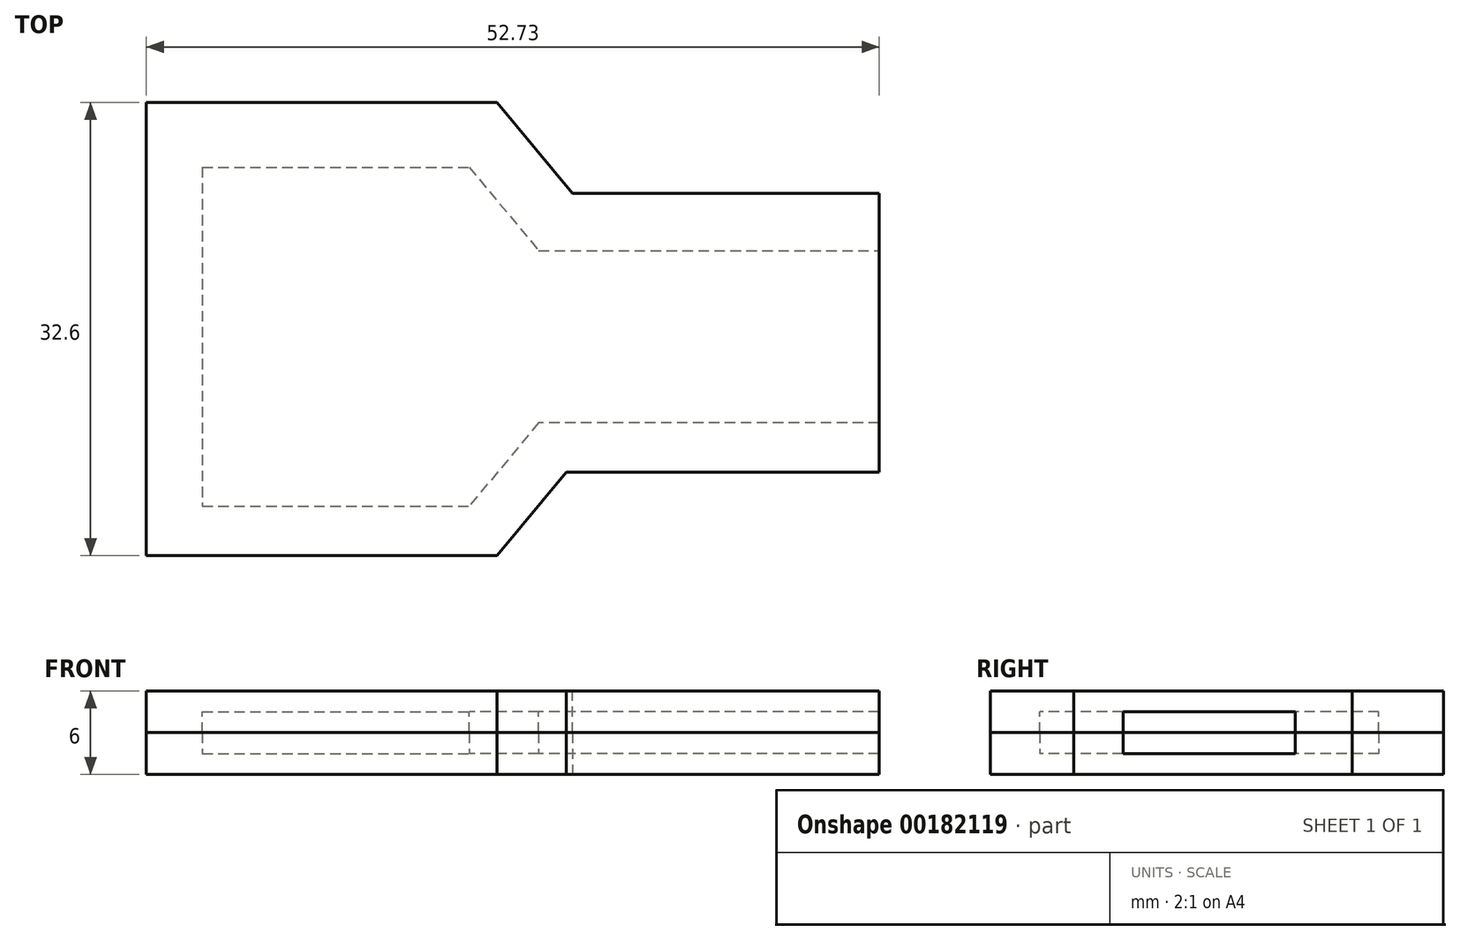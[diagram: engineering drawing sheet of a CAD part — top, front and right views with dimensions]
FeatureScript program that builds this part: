
annotation { "Feature Type Name" : "Feature", "Feature Type Description" : "" }
export const myFeature = defineFeature(function(context is Context, id is Id, definition is map)
    precondition{}
    {
        {
            var Q0;
            Q0=qCreatedBy(makeId("Top.planeOp"),FACE);
            var sketch = newSketch(context, id + "F0", { "sketchPlane" : qUnion([Q0])});
            skLineSegment(sketch, "E0", {"start": v(-24.2, 18.4) * mm, "end": v(-24.2, -6) * mm});
            skLineSegment(sketch, "E1", {"start": v(-24.2, -6) * mm, "end": v(-5, -6) * mm});
            skLineSegment(sketch, "E2", {"start": v(0, 0) * mm, "end": v(-5, -6) * mm});
            skLineSegment(sketch, "E3", {"start": v(-24.2, 18.4) * mm, "end": v(-5, 18.4) * mm});
            skLineSegment(sketch, "E4", {"start": v(-5, 18.4) * mm, "end": v(0, 12.4) * mm});
            skLineSegment(sketch, "E5", {"start": v(24.5, 0) * mm, "end": v(0, 0) * mm});
            skLineSegment(sketch, "E6", {"start": v(0, 12.4) * mm, "end": v(24.5, 12.4) * mm});
            skLineSegment(sketch, "E7", {"start": v(24.5, 12.4) * mm, "end": v(24.5, 0) * mm});
            skLineSegment(sketch, "E8.0", {"start": v(2.45, 16.5) * mm, "end": v(24.5, 16.5) * mm});
            skLineSegment(sketch, "E8.1", {"start": v(-3, 23.05) * mm, "end": v(2.45, 16.5) * mm});
            skLineSegment(sketch, "E8.3", {"start": v(-28.23, 23.05) * mm, "end": v(-3, 23.05) * mm});
            skLineSegment(sketch, "E8.4", {"start": v(24.5, -3.55) * mm, "end": v(2, -3.55) * mm});
            skLineSegment(sketch, "E8.5", {"start": v(2, -3.55) * mm, "end": v(-3, -9.55) * mm});
            skLineSegment(sketch, "E8.6", {"start": v(-28.23, -9.55) * mm, "end": v(-3, -9.55) * mm});
            skLineSegment(sketch, "E8.7", {"start": v(-28.23, 23.05) * mm, "end": v(-28.23, -9.55) * mm});
            skLineSegment(sketch, "E9", {"start": v(24.5, 16.5) * mm, "end": v(24.5, -3.55) * mm});
            skPoint(sketch, "E10.orphan", {"position": v(33, 0) * mm});
            skPoint(sketch, "E11.orphan", {"position": v(33, 12.4) * mm});
            skSolve(sketch);
        }
        {
            var Q0;
            Q0=makeQuery(id+"F0.imprint","IMPRINT",FACE,{"disambiguationData":[TD([[makeQuery(id+"F0.imprint","IMPRINT",EDGE,{"derivedFrom":sQuery(id+"F0.wireOp",EDGE,"E0")}),-1.0]])]});
            extrude(context, id + "F1", {"entities" : qUnion([Q0]), "depth" : 3 * mm});
        }
        {
            var Q0;
            Q0 = qSketchRegion(id + "F0", true);
            extrude(context, id + "F2", {"entities" : qUnion([Q0]), "operationType" : NewBodyOperationType.ADD, "depth" : 1.5 * mm});
        }
        {
            var Q0;
            Q0=makeQuery(id+"F1.opExtrude","SWEPT_BODY",BODY,{"disambiguationData":[OSD([sQuery(id+"F0.wireOp",EDGE,"E0"),sQuery(id+"F0.wireOp",EDGE,"E1"),sQuery(id+"F0.wireOp",EDGE,"E2"),sQuery(id+"F0.wireOp",EDGE,"E3"),sQuery(id+"F0.wireOp",EDGE,"E4"),sQuery(id+"F0.wireOp",EDGE,"E5"),sQuery(id+"F0.wireOp",EDGE,"E6"),sQuery(id+"F0.wireOp",EDGE,"E8.0"),sQuery(id+"F0.wireOp",EDGE,"E8.1"),sQuery(id+"F0.wireOp",EDGE,"E8.3"),sQuery(id+"F0.wireOp",EDGE,"E8.4"),sQuery(id+"F0.wireOp",EDGE,"E8.5"),sQuery(id+"F0.wireOp",EDGE,"E8.6"),sQuery(id+"F0.wireOp",EDGE,"E8.7"),sQuery(id+"F0.wireOp",EDGE,"E9")])]});
            var Q1;
            Q1=makeQuery(id+"F1.opExtrude","CAP_FACE",FACE,{"disambiguationData":[OSD([sQuery(id+"F0.wireOp",EDGE,"E0"),sQuery(id+"F0.wireOp",EDGE,"E1"),sQuery(id+"F0.wireOp",EDGE,"E2"),sQuery(id+"F0.wireOp",EDGE,"E3"),sQuery(id+"F0.wireOp",EDGE,"E4"),sQuery(id+"F0.wireOp",EDGE,"E5"),sQuery(id+"F0.wireOp",EDGE,"E6"),sQuery(id+"F0.wireOp",EDGE,"E8.0"),sQuery(id+"F0.wireOp",EDGE,"E8.1"),sQuery(id+"F0.wireOp",EDGE,"E8.3"),sQuery(id+"F0.wireOp",EDGE,"E8.4"),sQuery(id+"F0.wireOp",EDGE,"E8.5"),sQuery(id+"F0.wireOp",EDGE,"E8.6"),sQuery(id+"F0.wireOp",EDGE,"E8.7"),sQuery(id+"F0.wireOp",EDGE,"E9")])],"isStart":false});
            mirror(context, id + "F3", {"entities" : qUnion([Q0]), "mirrorPlane" : qUnion([Q1])});
        }
    });
